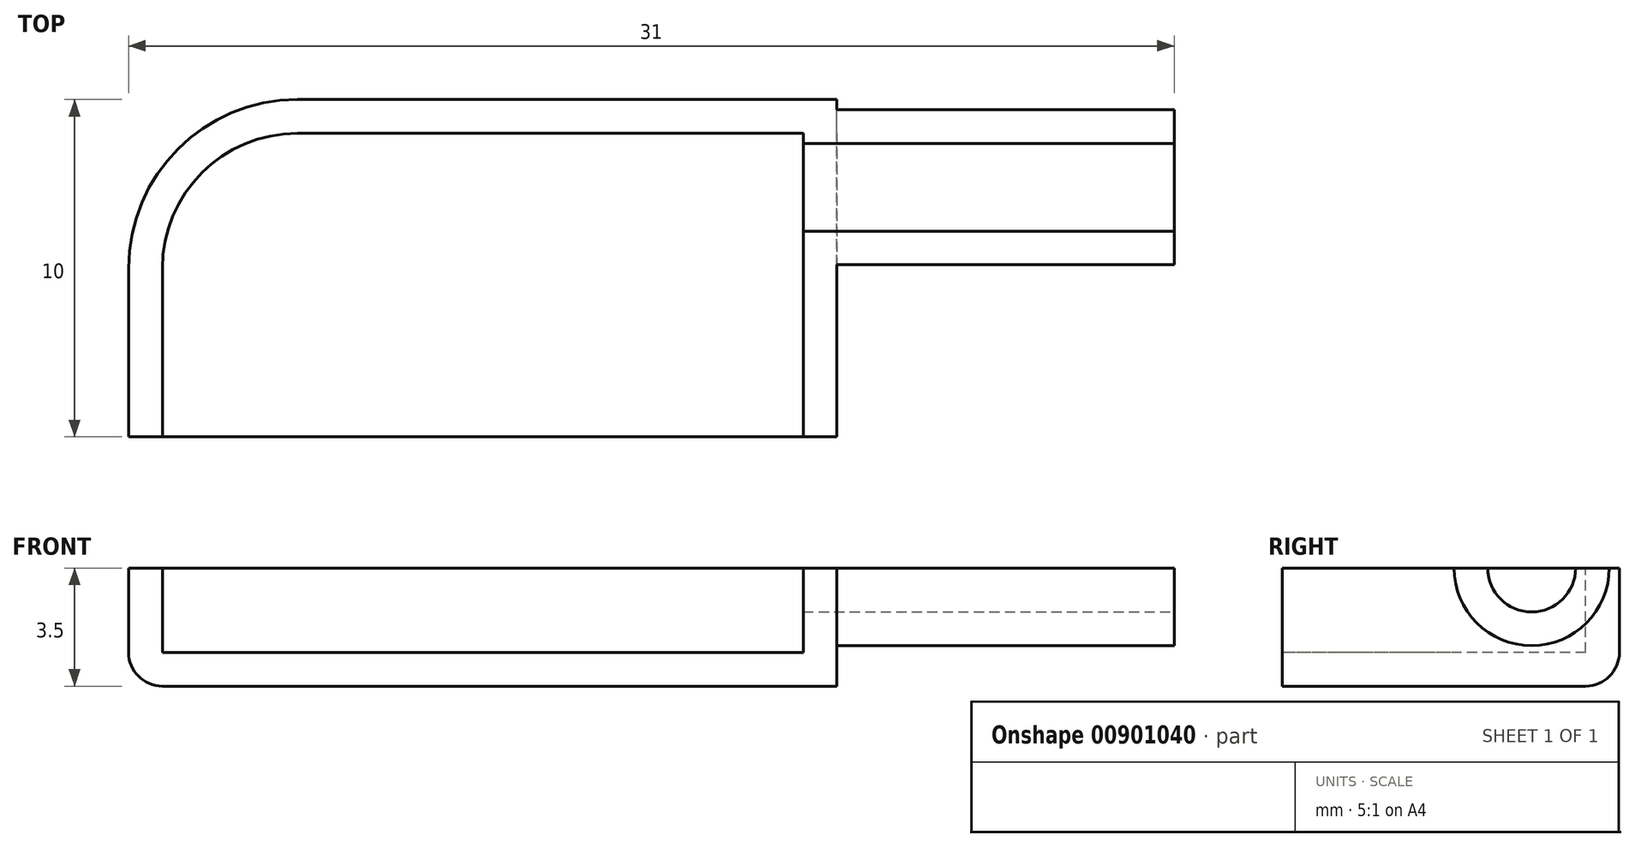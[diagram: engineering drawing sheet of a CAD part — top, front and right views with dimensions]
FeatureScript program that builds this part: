
annotation { "Feature Type Name" : "Feature", "Feature Type Description" : "" }
export const myFeature = defineFeature(function(context is Context, id is Id, definition is map)
    precondition{}
    {
        {
            var Q0;
            Q0=qCreatedBy(makeId("Top.planeOp"),FACE);
            var sketch = newSketch(context, id + "F0", { "sketchPlane" : qUnion([Q0])});
            skLineSegment(sketch, "E0.bottom", {"start": v(-4.03, 8.7) * mm, "end": v(11.97, 8.7) * mm});
            skLineSegment(sketch, "E0.top", {"start": v(-9.03, -1.3) * mm, "end": v(11.97, -1.3) * mm});
            skLineSegment(sketch, "E0.left", {"start": v(-9.03, 3.7) * mm, "end": v(-9.03, -1.3) * mm});
            skLineSegment(sketch, "E0.right", {"start": v(11.97, 8.7) * mm, "end": v(11.97, -1.3) * mm});
            skPoint(sketch, "E1.visualSharp", {"position": v(-9.03, 8.7) * mm});
            skArc(sketch, "E1.filletArc", {"start": v(-4.03, 8.7) * mm, "mid": v(-7.56, 7.23) * mm, "end": v(-9.03, 3.7) * mm});
            skSolve(sketch);
        }
        {
            var Q0;
            Q0 = qSketchRegion(id + "F0", true);
            extrude(context, id + "F1", {"entities" : qUnion([Q0]), "depth" : 3.5 * mm, "offsetDistance" : 25 * mm});
        }
        {
            var Q0;
            Q0=makeQuery(id+"F1.opExtrude","CAP_FACE",FACE,{"disambiguationData":[OSD([sQuery(id+"F0.wireOp",EDGE,"E0.bottom"),sQuery(id+"F0.wireOp",EDGE,"E0.top"),sQuery(id+"F0.wireOp",EDGE,"E0.left"),sQuery(id+"F0.wireOp",EDGE,"E0.right"),sQuery(id+"F0.wireOp",EDGE,"E1.filletArc")])],"isStart":false});
            var sketch = newSketch(context, id + "F2", { "sketchPlane" : qUnion([Q0])});
            skLineSegment(sketch, "E2.0", {"start": v(-8.03, 3.7) * mm, "end": v(-8.03, -1.3) * mm});
            skArc(sketch, "E2.1", {"start": v(-4.03, 7.7) * mm, "mid": v(-6.86, 6.52) * mm, "end": v(-8.03, 3.7) * mm});
            skLineSegment(sketch, "E2.2", {"start": v(-4.03, 7.7) * mm, "end": v(10.97, 7.7) * mm});
            skLineSegment(sketch, "E2.3", {"start": v(10.97, 7.7) * mm, "end": v(10.97, -1.3) * mm});
            skSolve(sketch);
        }
        {
            var Q0;
            {var subQ1=sQuery(id+"F2.wireOp",EDGE,"E2.0");Q0=makeQuery(id+"F2.imprint","IMPRINT",FACE,{"disambiguationData":[TD([[makeQuery(id+"F2.imprint","IMPRINT",EDGE,{"derivedFrom":subQ1}),1.0]])]});}
            extrude(context, id + "F3", {"entities" : qUnion([Q0]), "operationType" : NewBodyOperationType.REMOVE, "oppositeDirection" : true, "depth" : 2.5 * mm, "offsetDistance" : 25 * mm});
        }
        {
            var Q0;
            Q0=makeQuery(id+"F1.opExtrude","CAP_EDGE",EDGE,{"disambiguationData":[OSD([sQuery(id+"F0.wireOp",EDGE,"E0.bottom")])],"isStart":true});
            var Q1;
            Q1=makeQuery(id+"F1.opExtrude","CAP_EDGE",EDGE,{"disambiguationData":[OSD([sQuery(id+"F0.wireOp",EDGE,"E1.filletArc")])],"isStart":true});
            var Q2;
            Q2=makeQuery(id+"F1.opExtrude","CAP_EDGE",EDGE,{"disambiguationData":[OSD([sQuery(id+"F0.wireOp",EDGE,"E0.left")])],"isStart":true});
            fillet(context, id + "F4", {"entities" : qUnion([Q0, Q1, Q2]), "radius" : 1 * mm, "tangentPropagation" : true, "allowEdgeOverflow" : false});
        }
        {
            var Q0;
            Q0=makeQuery(id+"F1.opExtrude","SWEPT_FACE",FACE,{"disambiguationData":[OSD([sQuery(id+"F0.wireOp",EDGE,"E0.right")])]});
            var sketch = newSketch(context, id + "F5", { "sketchPlane" : qUnion([Q0])});
            skCircle(sketch, "E3", {"center": v(6.1, 3.5) * mm, "radius": 1.3 * mm});
            skSolve(sketch);
        }
        {
            var Q0;
            Q0 = qSketchRegion(id + "F5", true);
            extrude(context, id + "F6", {"entities" : qUnion([Q0]), "operationType" : NewBodyOperationType.REMOVE, "oppositeDirection" : true, "depth" : 7.7 * mm, "offsetDistance" : 25 * mm});
        }
        {
            var Q0;
            Q0=makeQuery(id+"F1.opExtrude","SWEPT_FACE",FACE,{"disambiguationData":[OSD([sQuery(id+"F0.wireOp",EDGE,"E0.right")])]});
            var sketch = newSketch(context, id + "F7", { "sketchPlane" : qUnion([Q0])});
            skCircle(sketch, "E4", {"center": v(6.1, 3.5) * mm, "radius": 1.3 * mm});
            skCircle(sketch, "E5", {"center": v(6.1, 3.5) * mm, "radius": 2.3 * mm});
            skSolve(sketch);
        }
        {
            var Q0;
            {var subQ0=sQuery(id+"F7.wireOp",EDGE,"E4");var subQ1=sQuery(id+"F0.wireOp",EDGE,"E0.bottom");var subQ2=sQuery(id+"F0.wireOp",EDGE,"E0.right");var subQ7=makeQuery(id+"F1.opExtrude","CAP_EDGE",EDGE,{"disambiguationData":[OSD([subQ2])],"isStart":false});var subQ8=makeQuery(id+"F6.boolean.opBoolean","SPLIT",EDGE,{"disambiguationData":[TD([makeQuery(id+"F1.opExtrude","SWEPT_FACE",FACE,{"disambiguationData":[OSD([subQ1])]})])],"derivedFrom":subQ7});var subQ9=makeQuery(id+"F7.imprint","INTERSECT",VERTEX,{"derivedFrom":[subQ8,subQ0]});Q0=makeQuery(id+"F7.imprint","IMPRINT",FACE,{"disambiguationData":[TD([[makeQuery(id+"F7.imprint","IMPRINT",EDGE,{"disambiguationData":[TD([[subQ9,1.0]])],"derivedFrom":subQ0}),-1.0]])]});}
            extrude(context, id + "F8", {"entities" : qUnion([Q0]), "operationType" : NewBodyOperationType.ADD, "depth" : 10 * mm, "offsetDistance" : 25 * mm});
        }
    });
